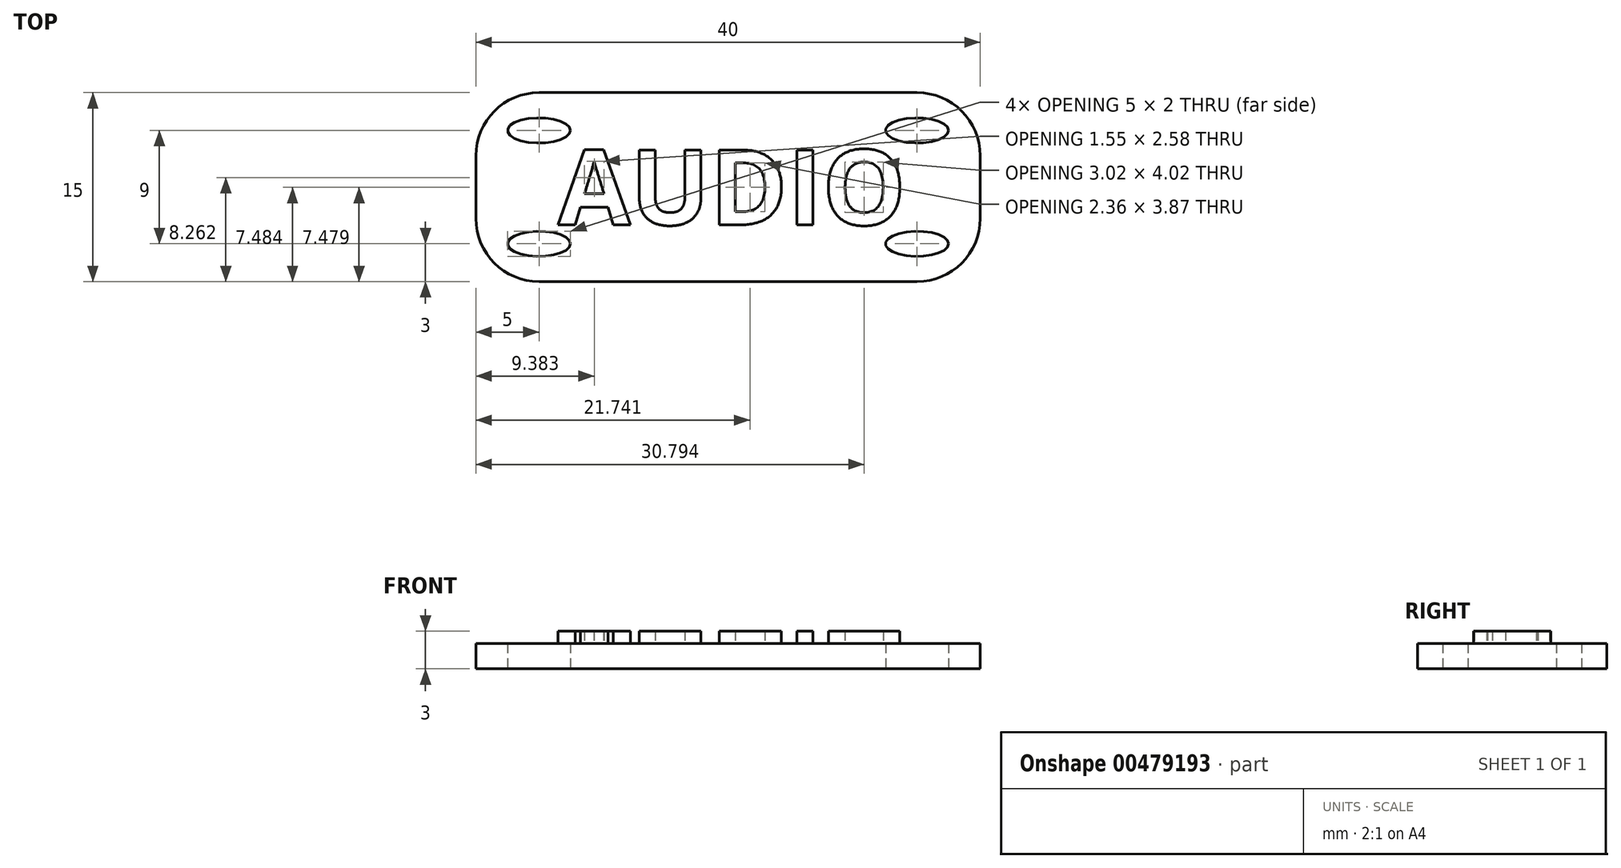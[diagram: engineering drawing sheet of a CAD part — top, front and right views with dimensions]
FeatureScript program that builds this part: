
annotation { "Feature Type Name" : "Feature", "Feature Type Description" : "" }
export const myFeature = defineFeature(function(context is Context, id is Id, definition is map)
    precondition{}
    {
        {
            var Q0;
            Q0=qCreatedBy(makeId("Top.planeOp"),FACE);
            var sketch = newSketch(context, id + "F0", { "sketchPlane" : qUnion([Q0])});
            skLineSegment(sketch, "E0.bottom", {"start": v(20, -7.5) * mm, "end": v(-20, -7.5) * mm});
            skLineSegment(sketch, "E0.top", {"start": v(20, 7.5) * mm, "end": v(-20, 7.5) * mm});
            skLineSegment(sketch, "E0.left", {"start": v(20, -7.5) * mm, "end": v(20, 7.5) * mm});
            skLineSegment(sketch, "E0.right", {"start": v(-20, -7.5) * mm, "end": v(-20, 7.5) * mm});
            skPoint(sketch, "E0.middle", {"position": v(0, 0) * mm});
            skLineSegment(sketch, "E1", {"start": v(-20, -4.5) * mm, "end": v(20, -4.5) * mm, "construction": true});
            skPoint(sketch, "E2", {"position": v(-15, -4.5) * mm});
            skEllipse(sketch, "E3", {"center": v(-15, -4.5) * mm, "majorRadius": 2.5 * mm, "minorRadius": 1 * mm, "majorAxis": v(1, 0)});
            skEllipse(sketch, "E4.1.0.0", {"center": v(15, -4.5) * mm, "majorRadius": 2.5 * mm, "minorRadius": 1 * mm, "majorAxis": v(1, 0)});
            skLineSegment(sketch, "E4.direction1", {"start": v(-15, -4.5) * mm, "end": v(15, -4.5) * mm, "construction": true});
            skLineSegment(sketch, "E5", {"start": v(20, 0) * mm, "end": v(-20, 0) * mm, "construction": true});
            skEllipse(sketch, "E6.MirrorC", {"center": v(15, 4.5) * mm, "majorRadius": 2.5 * mm, "minorRadius": 1 * mm, "majorAxis": v(1, 0)});
            skEllipse(sketch, "E7.MirrorC", {"center": v(-15, 4.5) * mm, "majorRadius": 2.5 * mm, "minorRadius": 1 * mm, "majorAxis": v(1, 0)});
            skSolve(sketch);
        }
        {
            var Q0;
            Q0=makeQuery(id+"F0.imprint","IMPRINT",FACE,{"disambiguationData":[TD([[makeQuery(id+"F0.imprint","IMPRINT",EDGE,{"derivedFrom":sQuery(id+"F0.wireOp",EDGE,"E0.bottom")}),-1.0]])]});
            extrude(context, id + "F1", {"entities" : qUnion([Q0]), "depth" : 2 * mm});
        }
        {
            var Q0;
            Q0=makeQuery(id+"F1.opExtrude","CAP_FACE",FACE,{"disambiguationData":[OSD([sQuery(id+"F0.wireOp",EDGE,"E0.bottom"),sQuery(id+"F0.wireOp",EDGE,"E0.top"),sQuery(id+"F0.wireOp",EDGE,"E0.left"),sQuery(id+"F0.wireOp",EDGE,"E0.right"),sQuery(id+"F0.wireOp",EDGE,"E3"),sQuery(id+"F0.wireOp",EDGE,"E4.1.0.0"),sQuery(id+"F0.wireOp",EDGE,"E6.MirrorC"),sQuery(id+"F0.wireOp",EDGE,"E7.MirrorC")])],"isStart":false});
            var sketch = newSketch(context, id + "F2", { "sketchPlane" : qUnion([Q0])});
            skText(sketch, "E8", { "text": "AUDIO", "fontName": "OpenSans-Bold.ttf"});
            const initialGuessF2  = {"E8": [-0.0135, -0.003, 1, 0, 0.006]};
            skSetInitialGuess(sketch, initialGuessF2);
            skSolve(sketch);
        }
        {
            var Q0;
            Q0=qSketchRegion(id+"F2",true);
            extrude(context, id + "F3", {"entities" : qUnion([Q0]), "depth" : 1 * mm});
        }
        {
            var Q0;
            Q0=makeQuery(id+"F1.opExtrude","SWEPT_EDGE",EDGE,{"disambiguationData":[OSD([sQuery(id+"F0.wireOp",EDGE,"E0.bottom"),sQuery(id+"F0.wireOp",EDGE,"E0.right")])]});
            var Q1;
            Q1=makeQuery(id+"F1.opExtrude","SWEPT_EDGE",EDGE,{"disambiguationData":[OSD([sQuery(id+"F0.wireOp",EDGE,"E0.bottom"),sQuery(id+"F0.wireOp",EDGE,"E0.left")])]});
            var Q2;
            Q2=makeQuery(id+"F1.opExtrude","SWEPT_EDGE",EDGE,{"disambiguationData":[OSD([sQuery(id+"F0.wireOp",EDGE,"E0.top"),sQuery(id+"F0.wireOp",EDGE,"E0.left")])]});
            var Q3;
            Q3=makeQuery(id+"F1.opExtrude","SWEPT_EDGE",EDGE,{"disambiguationData":[OSD([sQuery(id+"F0.wireOp",EDGE,"E0.top"),sQuery(id+"F0.wireOp",EDGE,"E0.right")])]});
            fillet(context, id + "F4", {"entities" : qUnion([Q0, Q1, Q2, Q3]), "radius" : 5 * mm, "tangentPropagation" : true, "allowEdgeOverflow" : false});
        }
    });
